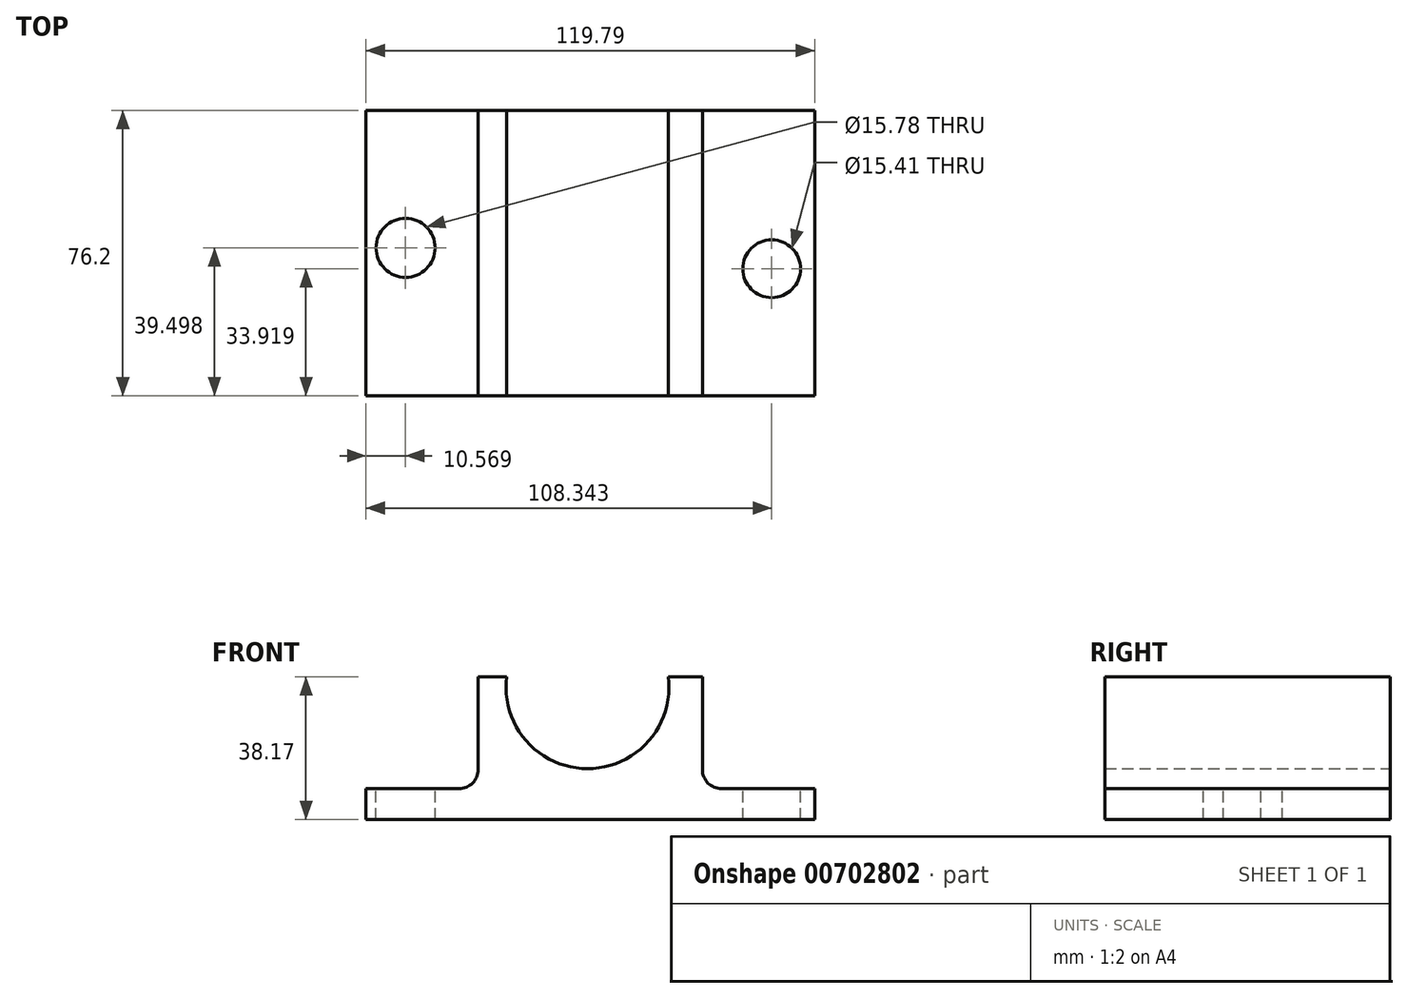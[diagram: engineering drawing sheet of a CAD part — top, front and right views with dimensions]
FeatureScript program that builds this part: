
annotation { "Feature Type Name" : "Feature", "Feature Type Description" : "" }
export const myFeature = defineFeature(function(context is Context, id is Id, definition is map)
    precondition{}
    {
        {
            var Q0;
            Q0=qCreatedBy(makeId("Front.planeOp"),FACE);
            var sketch = newSketch(context, id + "F0", { "sketchPlane" : qUnion([Q0])});
            skLineSegment(sketch, "E0", {"start": v(-63.86, -21.73) * mm, "end": v(55.93, -21.73) * mm});
            skLineSegment(sketch, "E1", {"start": v(55.93, -21.73) * mm, "end": v(55.93, -13.5) * mm});
            skLineSegment(sketch, "E2", {"start": v(55.93, -13.5) * mm, "end": v(25.98, -13.5) * mm});
            skLineSegment(sketch, "E3", {"start": v(25.98, -13.5) * mm, "end": v(25.98, 16.44) * mm});
            skLineSegment(sketch, "E4", {"start": v(25.98, 16.44) * mm, "end": v(16.88, 16.44) * mm});
            skLineSegment(sketch, "E5", {"start": v(-63.86, -21.73) * mm, "end": v(-63.86, -13.5) * mm});
            skLineSegment(sketch, "E6", {"start": v(-63.86, -13.5) * mm, "end": v(-33.91, -13.5) * mm});
            skLineSegment(sketch, "E7", {"start": v(-33.91, -13.5) * mm, "end": v(-33.91, 16.44) * mm});
            skLineSegment(sketch, "E8", {"start": v(-33.91, 16.44) * mm, "end": v(-26.28, 16.44) * mm});
            skArc(sketch, "E9", {"start": v(-26.28, 16.44) * mm, "mid": v(-4.7, -8.15) * mm, "end": v(16.88, 16.44) * mm});
            skSolve(sketch);
        }
        {
            var Q0;
            Q0 = qSketchRegion(id + "F0", true);
            extrude(context, id + "F1", {"entities" : qUnion([Q0]), "depth" : 76.2 * mm, "offsetDistance" : 25.4 * mm});
        }
        {
            var Q0;
            Q0=makeQuery(id+"F1.opExtrude","SWEPT_EDGE",EDGE,{"disambiguationData":[OSD([sQuery(id+"F0.wireOp",EDGE,"E6"),sQuery(id+"F0.wireOp",EDGE,"E7")])]});
            var Q1;
            Q1=makeQuery(id+"F1.opExtrude","SWEPT_EDGE",EDGE,{"disambiguationData":[OSD([sQuery(id+"F0.wireOp",EDGE,"E2"),sQuery(id+"F0.wireOp",EDGE,"E3")])]});
            fillet(context, id + "F2", {"entities" : qUnion([Q0, Q1]), "radius" : 5.08 * mm, "tangentPropagation" : true, "allowEdgeOverflow" : false});
        }
        {
            var Q0;
            Q0=makeQuery(id+"F1.opExtrude","SWEPT_FACE",FACE,{"disambiguationData":[OSD([sQuery(id+"F0.wireOp",EDGE,"E2")])]});
            var sketch = newSketch(context, id + "F3", { "sketchPlane" : qUnion([Q0])});
            skCircle(sketch, "E10", {"center": v(44.48, -42.28) * mm, "radius": 7.7 * mm});
            skCircle(sketch, "E11", {"center": v(-53.3, -36.7) * mm, "radius": 7.89 * mm});
            skSolve(sketch);
        }
        {
            var Q0;
            Q0 = qSketchRegion(id + "F3", true);
            extrude(context, id + "F4", {"entities" : qUnion([Q0]), "operationType" : NewBodyOperationType.REMOVE, "oppositeDirection" : true, "depth" : 25.4 * mm, "offsetDistance" : 25.4 * mm});
        }
    });
